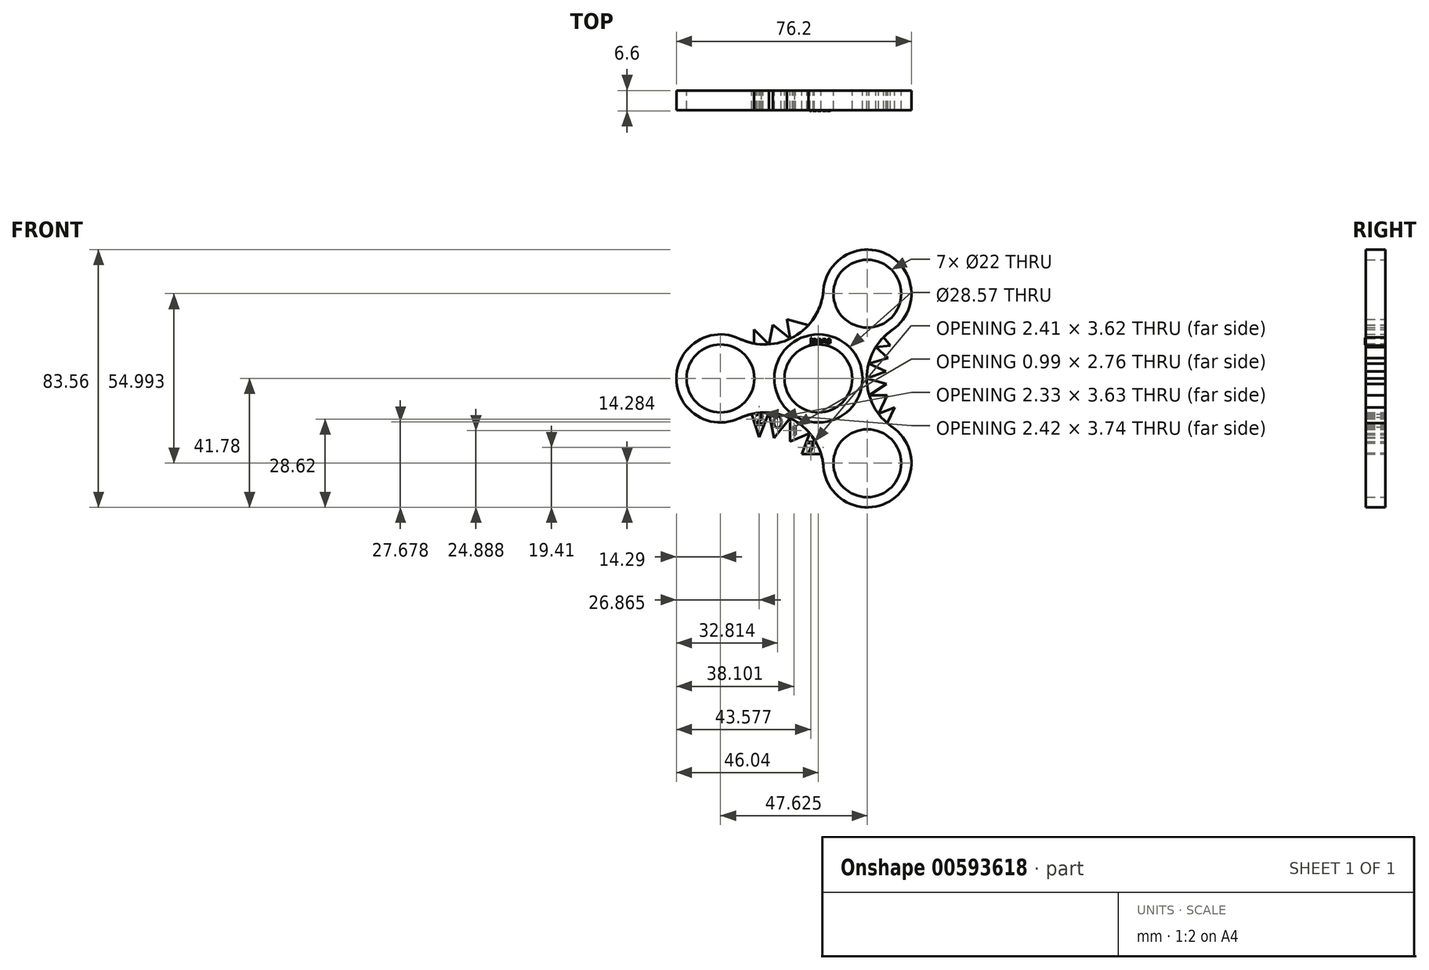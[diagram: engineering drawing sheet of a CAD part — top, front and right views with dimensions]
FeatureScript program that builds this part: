
annotation { "Feature Type Name" : "Feature", "Feature Type Description" : "" }
export const myFeature = defineFeature(function(context is Context, id is Id, definition is map)
    precondition{}
    {
        {
            var Q0;
            Q0=qCreatedBy(makeId("Front.planeOp"),FACE);
            var sketch = newSketch(context, id + "F0", { "sketchPlane" : qUnion([Q0])});
            skCircle(sketch, "E0", {"center": v(0, 0) * mm, "radius": 14.29 * mm});
            skCircle(sketch, "E1", {"center": v(0, 0) * mm, "radius": 11 * mm});
            skCircle(sketch, "E2", {"center": v(-31.75, 0) * mm, "radius": 14.29 * mm});
            skCircle(sketch, "E3", {"center": v(-31.75, 0) * mm, "radius": 11 * mm});
            skCircle(sketch, "E4.1.0", {"center": v(15.87, -27.5) * mm, "radius": 11 * mm});
            skCircle(sketch, "E4.1.1", {"center": v(15.87, -27.5) * mm, "radius": 14.29 * mm});
            skCircle(sketch, "E4.2.0", {"center": v(15.88, 27.5) * mm, "radius": 11 * mm});
            skCircle(sketch, "E4.2.1", {"center": v(15.88, 27.5) * mm, "radius": 14.29 * mm});
            skCircle(sketch, "E5", {"center": v(-17.36, 30.07) * mm, "radius": 19.05 * mm});
            skCircle(sketch, "E6", {"center": v(-17.36, -30.07) * mm, "radius": 19.05 * mm});
            skCircle(sketch, "E7", {"center": v(34.73, 0) * mm, "radius": 19.05 * mm});
            skSolve(sketch);
        }
        {
            var Q0;
            Q0=makeQuery(id+"F0.imprint","IMPRINT",FACE,{"disambiguationData":[TD([[makeQuery(id+"F0.imprint","IMPRINT",EDGE,{"derivedFrom":sQuery(id+"F0.wireOp",EDGE,"E1")}),1.0]])]});
            var sketch = newSketch(context, id + "F1", { "sketchPlane" : qUnion([Q0])});
            skCircle(sketch, "E8.0", {"center": v(0, 0) * mm, "radius": 14.29 * mm});
            skCircle(sketch, "E8.1", {"center": v(0, 0) * mm, "radius": 11 * mm});
            skCircle(sketch, "E8.2", {"center": v(-31.75, 0) * mm, "radius": 11 * mm});
            skCircle(sketch, "E8.3", {"center": v(15.87, -27.5) * mm, "radius": 11 * mm});
            skCircle(sketch, "E8.4", {"center": v(15.87, -27.5) * mm, "radius": 14.29 * mm});
            skCircle(sketch, "E8.5", {"center": v(15.88, 27.5) * mm, "radius": 11 * mm});
            skCircle(sketch, "E8.6", {"center": v(15.88, 27.5) * mm, "radius": 14.29 * mm});
            skArc(sketch, "E8.7", {"start": v(-25.58, 12.89) * mm, "mid": v(-7.2, 13.96) * mm, "end": v(1.69, 30.07) * mm});
            skArc(sketch, "E8.8", {"start": v(1.63, -28.6) * mm, "mid": v(-7.84, -13.58) * mm, "end": v(-25.58, -12.89) * mm});
            skArc(sketch, "E8.9", {"start": v(23.95, 15.71) * mm, "mid": v(15.68, 0) * mm, "end": v(23.95, -15.71) * mm});
            skCircle(sketch, "E9.0", {"center": v(-31.75, 0) * mm, "radius": 14.29 * mm});
            skLineSegment(sketch, "E10", {"start": v(-20.92, 11.36) * mm, "end": v(-20.92, 15.86) * mm});
            skLineSegment(sketch, "E11", {"start": v(-20.92, 15.86) * mm, "end": v(-16.03, 11.07) * mm});
            skLineSegment(sketch, "E12", {"start": v(-16.03, 11.07) * mm, "end": v(-14.75, 17.37) * mm});
            skLineSegment(sketch, "E13", {"start": v(-14.75, 17.37) * mm, "end": v(-9.14, 12.9) * mm});
            skLineSegment(sketch, "E14", {"start": v(-9.14, 12.9) * mm, "end": v(-10.14, 19.15) * mm});
            skLineSegment(sketch, "E15", {"start": v(-10.14, 19.15) * mm, "end": v(-3.2, 17.33) * mm});
            skLineSegment(sketch, "E16", {"start": v(-21.64, -11.5) * mm, "end": v(-19.23, -18.99) * mm});
            skLineSegment(sketch, "E17", {"start": v(-19.23, -18.99) * mm, "end": v(-16.02, -11.07) * mm});
            skLineSegment(sketch, "E18", {"start": v(-16.02, -11.07) * mm, "end": v(-14.4, -19.27) * mm});
            skLineSegment(sketch, "E19", {"start": v(-14.4, -19.27) * mm, "end": v(-9.14, -12.89) * mm});
            skLineSegment(sketch, "E20", {"start": v(-9.14, -12.89) * mm, "end": v(-9.14, -20.48) * mm});
            skLineSegment(sketch, "E21", {"start": v(-9.14, -20.48) * mm, "end": v(-2.85, -17.73) * mm});
            skLineSegment(sketch, "E22", {"start": v(-2.85, -17.73) * mm, "end": v(-5.43, -24.56) * mm});
            skLineSegment(sketch, "E23", {"start": v(-5.43, -24.56) * mm, "end": v(0.87, -24.56) * mm});
            skLineSegment(sketch, "E24", {"start": v(21.16, 13.38) * mm, "end": v(23.37, 10.61) * mm});
            skLineSegment(sketch, "E25", {"start": v(23.37, 10.61) * mm, "end": v(18.6, 10.15) * mm});
            skLineSegment(sketch, "E26", {"start": v(18.6, 10.15) * mm, "end": v(22.52, 6.56) * mm});
            skLineSegment(sketch, "E27", {"start": v(22.52, 6.56) * mm, "end": v(16.3, 4.81) * mm});
            skLineSegment(sketch, "E28", {"start": v(16.3, 4.81) * mm, "end": v(21.96, 2.23) * mm});
            skLineSegment(sketch, "E29", {"start": v(21.96, 2.23) * mm, "end": v(15.68, 0) * mm});
            skLineSegment(sketch, "E30", {"start": v(15.68, 0) * mm, "end": v(22.1, -1.72) * mm});
            skLineSegment(sketch, "E31", {"start": v(22.1, -1.72) * mm, "end": v(16.5, -5.51) * mm});
            skLineSegment(sketch, "E32", {"start": v(16.5, -5.51) * mm, "end": v(22.3, -5.51) * mm});
            skLineSegment(sketch, "E33", {"start": v(22.3, -5.51) * mm, "end": v(19.46, -11.4) * mm});
            skLineSegment(sketch, "E34", {"start": v(19.46, -11.4) * mm, "end": v(24.7, -9.41) * mm});
            skLineSegment(sketch, "E35", {"start": v(24.7, -9.41) * mm, "end": v(22.37, -14.5) * mm});
            skText(sketch, "E36", { "text": "2\n", "fontName": "OpenSans-Regular.ttf"});
            skText(sketch, "E37", { "text": "0\n", "fontName": "OpenSans-Regular.ttf"});
            skText(sketch, "E38", { "text": "1", "fontName": "OpenSans-Regular.ttf"});
            skText(sketch, "E39", { "text": "7", "fontName": "OpenSans-Regular.ttf"});
            const initialGuessF1  = {"E36": [-0.02064, -0.01503, 1, 0, 0.00372], "E37": [-0.01464, -0.01587, 1, 0, 0.00356], "E38": [-0.00879, -0.01827, 1, 0, 0.00278], "E39": [-0.0039, -0.02418, 1, 0, 0.00365]};
            skSetInitialGuess(sketch, initialGuessF1);
            skSolve(sketch);
        }
        {
            var Q0;
            Q0=makeQuery(id+"F0.imprint","IMPRINT",FACE,{"disambiguationData":[TD([[makeQuery(id+"F0.imprint","IMPRINT",EDGE,{"derivedFrom":sQuery(id+"F0.wireOp",EDGE,"E0")}),1.0]])]});
            var sketch = newSketch(context, id + "F2", { "sketchPlane" : qUnion([Q0])});
            skText(sketch, "E40", { "text": "Jenna", "fontName": "OpenSans-Regular.ttf"});
            const initialGuessF2  = {"E40": [-0.00268, 0.01138, 1, 0, 0.00188]};
            skSetInitialGuess(sketch, initialGuessF2);
            skSolve(sketch);
        }
        {
            var Q0;
            Q0=makeQuery(id+"F0.imprint","IMPRINT",FACE,{"disambiguationData":[TD([[makeQuery(id+"F0.imprint","IMPRINT",EDGE,{"derivedFrom":sQuery(id+"F0.wireOp",EDGE,"E3")}),-1.0]])]});
            var Q1;
            Q1=makeQuery(id+"F0.imprint","IMPRINT",FACE,{"disambiguationData":[TD([[makeQuery(id+"F0.imprint","IMPRINT",EDGE,{"derivedFrom":sQuery(id+"F0.wireOp",EDGE,"E0")}),1.0]])]});
            var Q2;
            Q2=makeQuery(id+"F0.imprint","IMPRINT",FACE,{"disambiguationData":[TD([[makeQuery(id+"F0.imprint","IMPRINT",EDGE,{"derivedFrom":sQuery(id+"F0.wireOp",EDGE,"E4.2.0")}),-1.0]])]});
            var Q3;
            Q3=makeQuery(id+"F0.imprint","IMPRINT",FACE,{"disambiguationData":[TD([[makeQuery(id+"F0.imprint","IMPRINT",EDGE,{"derivedFrom":sQuery(id+"F0.wireOp",EDGE,"E4.1.0")}),-1.0]])]});
            var Q4;
            Q4 = qSketchRegion(id + "F1", true);
            var Q5;
            Q5=makeQuery(id+"F0.imprint","IMPRINT",FACE,{"disambiguationData":[TD([[makeQuery(id+"F0.imprint","IMPRINT",EDGE,{"derivedFrom":sQuery(id+"F0.wireOp",EDGE,"E0")}),-1.0]])]});
            extrude(context, id + "F3", {"entities" : qUnion([Q0, Q1, Q2, Q3, Q4, Q5]), "depth" : 6.35 * mm, "offsetDistance" : 25.4 * mm});
        }
        {
            var Q0;
            Q0 = qSketchRegion(id + "F2", true);
            extrude(context, id + "F4", {"entities" : qUnion([Q0]), "operationType" : NewBodyOperationType.ADD, "depth" : 6.6 * mm, "offsetDistance" : 25.4 * mm});
        }
    });
